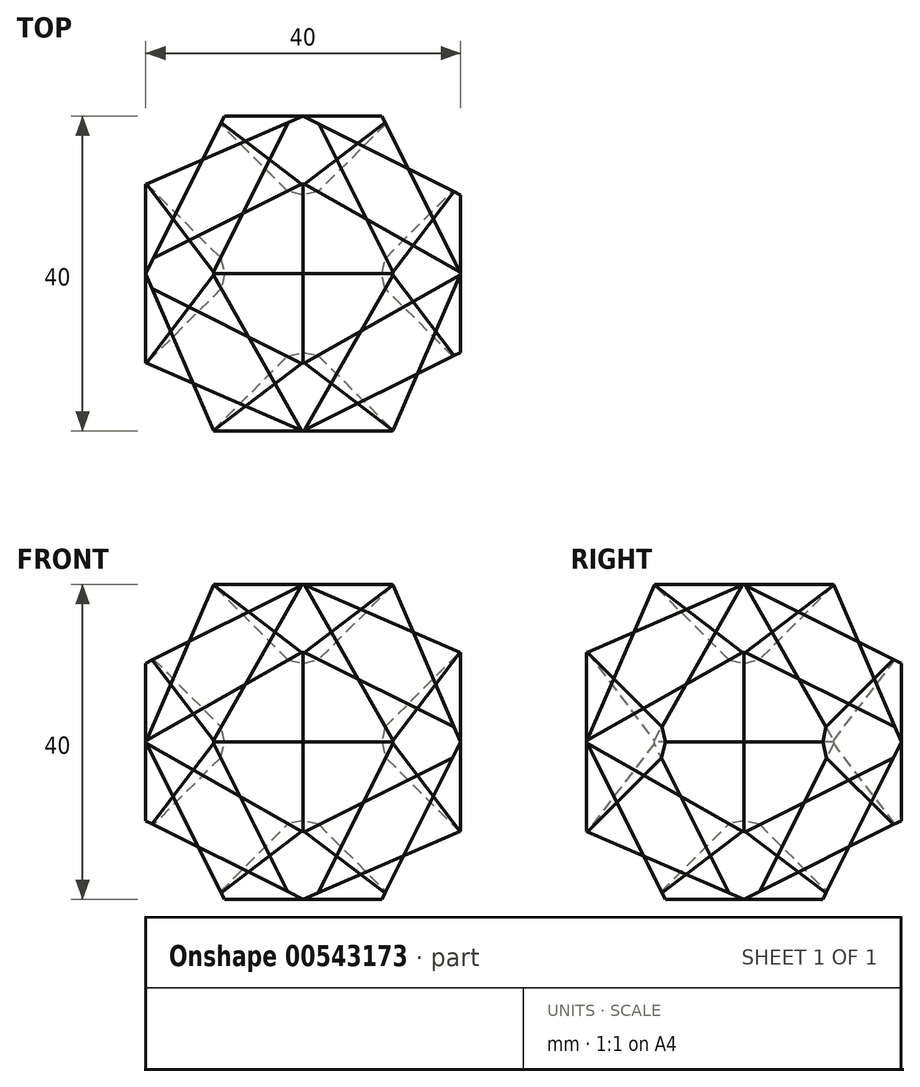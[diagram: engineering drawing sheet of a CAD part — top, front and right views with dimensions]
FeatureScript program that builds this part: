
annotation { "Feature Type Name" : "Feature", "Feature Type Description" : "" }
export const myFeature = defineFeature(function(context is Context, id is Id, definition is map)
    precondition{}
    {
        {
            var Q0;
            Q0=qCreatedBy(makeId("Front.planeOp"),FACE);
            var sketch = newSketch(context, id + "F0", { "sketchPlane" : qUnion([Q0])});
            skLineSegment(sketch, "E0", {"start": v(46.28, 0) * mm, "end": v(0, 20) * mm});
            skLineSegment(sketch, "E1", {"start": v(0, 20) * mm, "end": v(-40, 0) * mm});
            skLineSegment(sketch, "E2", {"start": v(-40, 0) * mm, "end": v(0, -20) * mm});
            skLineSegment(sketch, "E3", {"start": v(0, -20) * mm, "end": v(46.28, 0) * mm});
            skSolve(sketch);
        }
        {
            var Q0;
            Q0=makeQuery(id+"F0.imprint","IMPRINT",FACE,{"disambiguationData":[TD([[makeQuery(id+"F0.imprint","IMPRINT",EDGE,{"derivedFrom":sQuery(id+"F0.wireOp",EDGE,"E0")}),1.0]])]});
            extrude(context, id + "F1", {"entities" : qUnion([Q0]), "depth" : 25 * mm, "offsetDistance" : 25 * mm, "hasSecondDirection" : true, "secondDirectionOppositeDirection" : true, "secondDirectionDepth" : 25 * mm});
        }
        {
            var Q0;
            Q0=qCreatedBy(makeId("Front.planeOp"),FACE);
            var sketch = newSketch(context, id + "F2", { "sketchPlane" : qUnion([Q0])});
            skLineSegment(sketch, "E4", {"start": v(0, 49.78) * mm, "end": v(0, 0) * mm});
            skSolve(sketch);
        }
        {
            var Q0;
            Q0=qCreatedBy(makeId("Front.planeOp"),FACE);
            var sketch = newSketch(context, id + "F3", { "sketchPlane" : qUnion([Q0])});
            skLineSegment(sketch, "E5", {"start": v(60.84, 0) * mm, "end": v(0, 0) * mm});
            skSolve(sketch);
        }
        {
            var Q0;
            Q0=qCreatedBy(makeId("Right.planeOp"),FACE);
            var sketch = newSketch(context, id + "F4", { "sketchPlane" : qUnion([Q0])});
            skLineSegment(sketch, "E6", {"start": v(48.72, 0) * mm, "end": v(-1.84, 0) * mm});
            skSolve(sketch);
        }
        {
            var Q0;
            Q0=makeQuery(id+"F1.opExtrude","SWEPT_BODY",BODY,{"disambiguationData":[OSD([sQuery(id+"F0.wireOp",EDGE,"E0"),sQuery(id+"F0.wireOp",EDGE,"E1"),sQuery(id+"F0.wireOp",EDGE,"E2"),sQuery(id+"F0.wireOp",EDGE,"E3")])]});
            var Q1;
            Q1=sQuery(id+"F2.wireOp",EDGE,"E4");
            transform(context, id + "F5", {"entities" : qUnion([Q0]), "transformType" : TransformType.ROTATION, "transformAxis" : qUnion([Q1]), "angle" : 90 * degree, "makeCopy" : true});
        }
        {
            var Q0;
            Q0=makeQuery(id+"F5.opPattern","COPY",BODY,{"derivedFrom":makeQuery(id+"F1.opExtrude","SWEPT_BODY",BODY,{"disambiguationData":[OSD([sQuery(id+"F0.wireOp",EDGE,"E0"),sQuery(id+"F0.wireOp",EDGE,"E1"),sQuery(id+"F0.wireOp",EDGE,"E2"),sQuery(id+"F0.wireOp",EDGE,"E3")])]}),"instanceName":"1"});
            var Q1;
            Q1=sQuery(id+"F4.wireOp",EDGE,"E6");
            transform(context, id + "F6", {"entities" : qUnion([Q0]), "transformType" : TransformType.ROTATION, "transformAxis" : qUnion([Q1]), "angle" : 90 * degree, "makeCopy" : true});
        }
        {
            var Q0;
            Q0=makeQuery(id+"F5.opPattern","COPY",BODY,{"derivedFrom":makeQuery(id+"F1.opExtrude","SWEPT_BODY",BODY,{"disambiguationData":[OSD([sQuery(id+"F0.wireOp",EDGE,"E0"),sQuery(id+"F0.wireOp",EDGE,"E1"),sQuery(id+"F0.wireOp",EDGE,"E2"),sQuery(id+"F0.wireOp",EDGE,"E3")])]}),"instanceName":"1"});
            var Q1;
            Q1=sQuery(id+"F3.wireOp",EDGE,"E5");
            transform(context, id + "F7", {"entities" : qUnion([Q0]), "transformType" : TransformType.ROTATION, "transformAxis" : qUnion([Q1]), "angle" : 90 * degree, "makeCopy" : false});
        }
        {
            var Q0;
            Q0=makeQuery(id+"F5.opPattern","COPY",BODY,{"derivedFrom":makeQuery(id+"F1.opExtrude","SWEPT_BODY",BODY,{"disambiguationData":[OSD([sQuery(id+"F0.wireOp",EDGE,"E0"),sQuery(id+"F0.wireOp",EDGE,"E1"),sQuery(id+"F0.wireOp",EDGE,"E2"),sQuery(id+"F0.wireOp",EDGE,"E3")])]}),"instanceName":"1"});
            var Q1;
            Q1=makeQuery(id+"F6.opPattern","COPY",BODY,{"derivedFrom":makeQuery(id+"F5.opPattern","COPY",BODY,{"derivedFrom":makeQuery(id+"F1.opExtrude","SWEPT_BODY",BODY,{"disambiguationData":[OSD([sQuery(id+"F0.wireOp",EDGE,"E0"),sQuery(id+"F0.wireOp",EDGE,"E1"),sQuery(id+"F0.wireOp",EDGE,"E2"),sQuery(id+"F0.wireOp",EDGE,"E3")])]}),"instanceName":"1"}),"instanceName":"1"});
            booleanBodies(context, id + "F8", {"operationType" : BooleanOperationType.INTERSECTION, "tools" : qUnion([Q0, Q1])});
        }
        {
            var Q0;
            {var subQ0=makeQuery(id+"F5.opPattern","COPY",BODY,{"derivedFrom":makeQuery(id+"F1.opExtrude","SWEPT_BODY",BODY,{"disambiguationData":[OSD([sQuery(id+"F0.wireOp",EDGE,"E0"),sQuery(id+"F0.wireOp",EDGE,"E1"),sQuery(id+"F0.wireOp",EDGE,"E2"),sQuery(id+"F0.wireOp",EDGE,"E3")])]}),"instanceName":"1"});Q0=makeQuery(id+"F8.opBoolean","INTERSECT",BODY,{"derivedFrom":[subQ0,makeQuery(id+"F6.opPattern","COPY",BODY,{"derivedFrom":subQ0,"instanceName":"1"})]});}
            var Q1;
            Q1=makeQuery(id+"F1.opExtrude","SWEPT_BODY",BODY,{"disambiguationData":[OSD([sQuery(id+"F0.wireOp",EDGE,"E0"),sQuery(id+"F0.wireOp",EDGE,"E1"),sQuery(id+"F0.wireOp",EDGE,"E2"),sQuery(id+"F0.wireOp",EDGE,"E3")])]});
            booleanBodies(context, id + "F9", {"operationType" : BooleanOperationType.INTERSECTION, "tools" : qUnion([Q0, Q1])});
        }
        {
            var Q0;
            Q0=qCreatedBy(makeId("Top.planeOp"),FACE);
            var sketch = newSketch(context, id + "F10", { "sketchPlane" : qUnion([Q0])});
            skLineSegment(sketch, "E7", {"start": v(20, 0) * mm, "end": v(0, 20) * mm});
            skLineSegment(sketch, "E8", {"start": v(0, 20) * mm, "end": v(-20, 0) * mm});
            skLineSegment(sketch, "E9", {"start": v(-20, 0) * mm, "end": v(0, -20) * mm});
            skLineSegment(sketch, "E10", {"start": v(0, -20) * mm, "end": v(20, 0) * mm});
            skSolve(sketch);
        }
        {
            var Q0;
            Q0=qSketchRegion(id+"F10",true);
            extrude(context, id + "F11", {"entities" : qUnion([Q0]), "depth" : 20 * mm, "offsetDistance" : 25 * mm, "hasDraft" : true, "draftAngle" : atan(1 / sqrt(2)), "draftPullDirection" : true, "hasSecondDirection" : true, "secondDirectionOppositeDirection" : true, "secondDirectionDepth" : 20 * mm, "hasSecondDirectionDraft" : true, "secondDirectionDraftAngle" : atan(1 / sqrt(2)), "secondDirectionDraftPullDirection" : true});
        }
        {
            var Q0;
            {var subQ0=makeQuery(id+"F1.opExtrude","SWEPT_BODY",BODY,{"disambiguationData":[OSD([sQuery(id+"F0.wireOp",EDGE,"E0"),sQuery(id+"F0.wireOp",EDGE,"E1"),sQuery(id+"F0.wireOp",EDGE,"E2"),sQuery(id+"F0.wireOp",EDGE,"E3")])]});var subQ1=makeQuery(id+"F5.opPattern","COPY",BODY,{"derivedFrom":subQ0,"instanceName":"1"});Q0=makeQuery(id+"F9.opBoolean","INTERSECT",BODY,{"derivedFrom":[subQ0,makeQuery(id+"F8.opBoolean","INTERSECT",BODY,{"derivedFrom":[subQ1,makeQuery(id+"F6.opPattern","COPY",BODY,{"derivedFrom":subQ1,"instanceName":"1"})]})]});}
            transform(context, id + "F12", {"entities" : qUnion([Q0]), "transformType" : TransformType.TRANSLATION_3D, "dx" : 50 * mm, "dy" : 0 * mm, "dz" : 0 * mm, "makeCopy" : false});
        }
        {
            var Q0;
            Q0=makeQuery(id+"F11.*.split.splitOp","SPLIT",BODY,{"derivedFrom":makeQuery(id+"F11.opExtrude","SWEPT_BODY",BODY,{"disambiguationData":[OSD([sQuery(id+"F10.wireOp",EDGE,"E7"),sQuery(id+"F10.wireOp",EDGE,"E8"),sQuery(id+"F10.wireOp",EDGE,"E9"),sQuery(id+"F10.wireOp",EDGE,"E10")])]})});
            var Q1;
            Q1=qCreatedBy(makeId("Origin.pointOp"),VERTEX);
            transform(context, id + "F13", {"entities" : qUnion([Q0]), "transformType" : TransformType.SCALE_UNIFORMLY, "scale" : 1.5, "scalePoint" : qUnion([Q1]), "makeCopy" : false});
        }
        {
            var Q0;
            {var subQ0=makeQuery(id+"F1.opExtrude","SWEPT_BODY",BODY,{"disambiguationData":[OSD([sQuery(id+"F0.wireOp",EDGE,"E0"),sQuery(id+"F0.wireOp",EDGE,"E1"),sQuery(id+"F0.wireOp",EDGE,"E2"),sQuery(id+"F0.wireOp",EDGE,"E3")])]});var subQ1=makeQuery(id+"F5.opPattern","COPY",BODY,{"derivedFrom":subQ0,"instanceName":"1"});Q0=makeQuery(id+"F9.opBoolean","INTERSECT",BODY,{"derivedFrom":[subQ0,makeQuery(id+"F8.opBoolean","INTERSECT",BODY,{"derivedFrom":[subQ1,makeQuery(id+"F6.opPattern","COPY",BODY,{"derivedFrom":subQ1,"instanceName":"1"})]})]});}
            transform(context, id + "F14", {"entities" : qUnion([Q0]), "transformType" : TransformType.TRANSLATION_3D, "dx" : -50 * mm, "dy" : 0 * mm, "dz" : 0 * mm, "makeCopy" : false});
        }
        {
            var Q0;
            Q0=makeQuery(id+"F11.*.split.splitOp","SPLIT",BODY,{"derivedFrom":makeQuery(id+"F11.opExtrude","SWEPT_BODY",BODY,{"disambiguationData":[OSD([sQuery(id+"F10.wireOp",EDGE,"E7"),sQuery(id+"F10.wireOp",EDGE,"E8"),sQuery(id+"F10.wireOp",EDGE,"E9"),sQuery(id+"F10.wireOp",EDGE,"E10")])]})});
            var Q1;
            Q1=qCreatedBy(makeId("Origin.pointOp"),VERTEX);
            transform(context, id + "F15", {"entities" : qUnion([Q0]), "transformType" : TransformType.SCALE_UNIFORMLY, "scale" : 1.05, "scalePoint" : qUnion([Q1]), "makeCopy" : false});
        }
        {
            var Q0;
            Q0=makeQuery(id+"F11.*.split.splitOp","SPLIT",BODY,{"derivedFrom":makeQuery(id+"F11.opExtrude","SWEPT_BODY",BODY,{"disambiguationData":[OSD([sQuery(id+"F10.wireOp",EDGE,"E7"),sQuery(id+"F10.wireOp",EDGE,"E8"),sQuery(id+"F10.wireOp",EDGE,"E9"),sQuery(id+"F10.wireOp",EDGE,"E10")])]})});
            var Q1;
            {var subQ0=makeQuery(id+"F1.opExtrude","SWEPT_BODY",BODY,{"disambiguationData":[OSD([sQuery(id+"F0.wireOp",EDGE,"E0"),sQuery(id+"F0.wireOp",EDGE,"E1"),sQuery(id+"F0.wireOp",EDGE,"E2"),sQuery(id+"F0.wireOp",EDGE,"E3")])]});var subQ1=makeQuery(id+"F5.opPattern","COPY",BODY,{"derivedFrom":subQ0,"instanceName":"1"});Q1=makeQuery(id+"F9.opBoolean","INTERSECT",BODY,{"derivedFrom":[subQ0,makeQuery(id+"F8.opBoolean","INTERSECT",BODY,{"derivedFrom":[subQ1,makeQuery(id+"F6.opPattern","COPY",BODY,{"derivedFrom":subQ1,"instanceName":"1"})]})]});}
            booleanBodies(context, id + "F16", {"operationType" : BooleanOperationType.INTERSECTION, "tools" : qUnion([Q0, Q1])});
        }
        {
            var Q0;
            {var subQ0=makeQuery(id+"F1.opExtrude","SWEPT_BODY",BODY,{"disambiguationData":[OSD([sQuery(id+"F0.wireOp",EDGE,"E0"),sQuery(id+"F0.wireOp",EDGE,"E1"),sQuery(id+"F0.wireOp",EDGE,"E2"),sQuery(id+"F0.wireOp",EDGE,"E3")])]});var subQ1=makeQuery(id+"F5.opPattern","COPY",BODY,{"derivedFrom":subQ0,"instanceName":"1"});Q0=makeQuery(id+"F16.opBoolean","INTERSECT",BODY,{"derivedFrom":[makeQuery(id+"F9.opBoolean","INTERSECT",BODY,{"derivedFrom":[subQ0,makeQuery(id+"F8.opBoolean","INTERSECT",BODY,{"derivedFrom":[subQ1,makeQuery(id+"F6.opPattern","COPY",BODY,{"derivedFrom":subQ1,"instanceName":"1"})]})]}),makeQuery(id+"F11.*.split.splitOp","SPLIT",BODY,{"derivedFrom":makeQuery(id+"F11.opExtrude","SWEPT_BODY",BODY,{"disambiguationData":[OSD([sQuery(id+"F10.wireOp",EDGE,"E7"),sQuery(id+"F10.wireOp",EDGE,"E8"),sQuery(id+"F10.wireOp",EDGE,"E9"),sQuery(id+"F10.wireOp",EDGE,"E10")])]})})]});}
            var Q1;
            Q1=sQuery(id+"F2.wireOp",EDGE,"E4");
            transform(context, id + "F17", {"entities" : qUnion([Q0]), "transformType" : TransformType.ROTATION, "transformAxis" : qUnion([Q1]), "angle" : 90 * degree, "makeCopy" : true});
        }
    });
